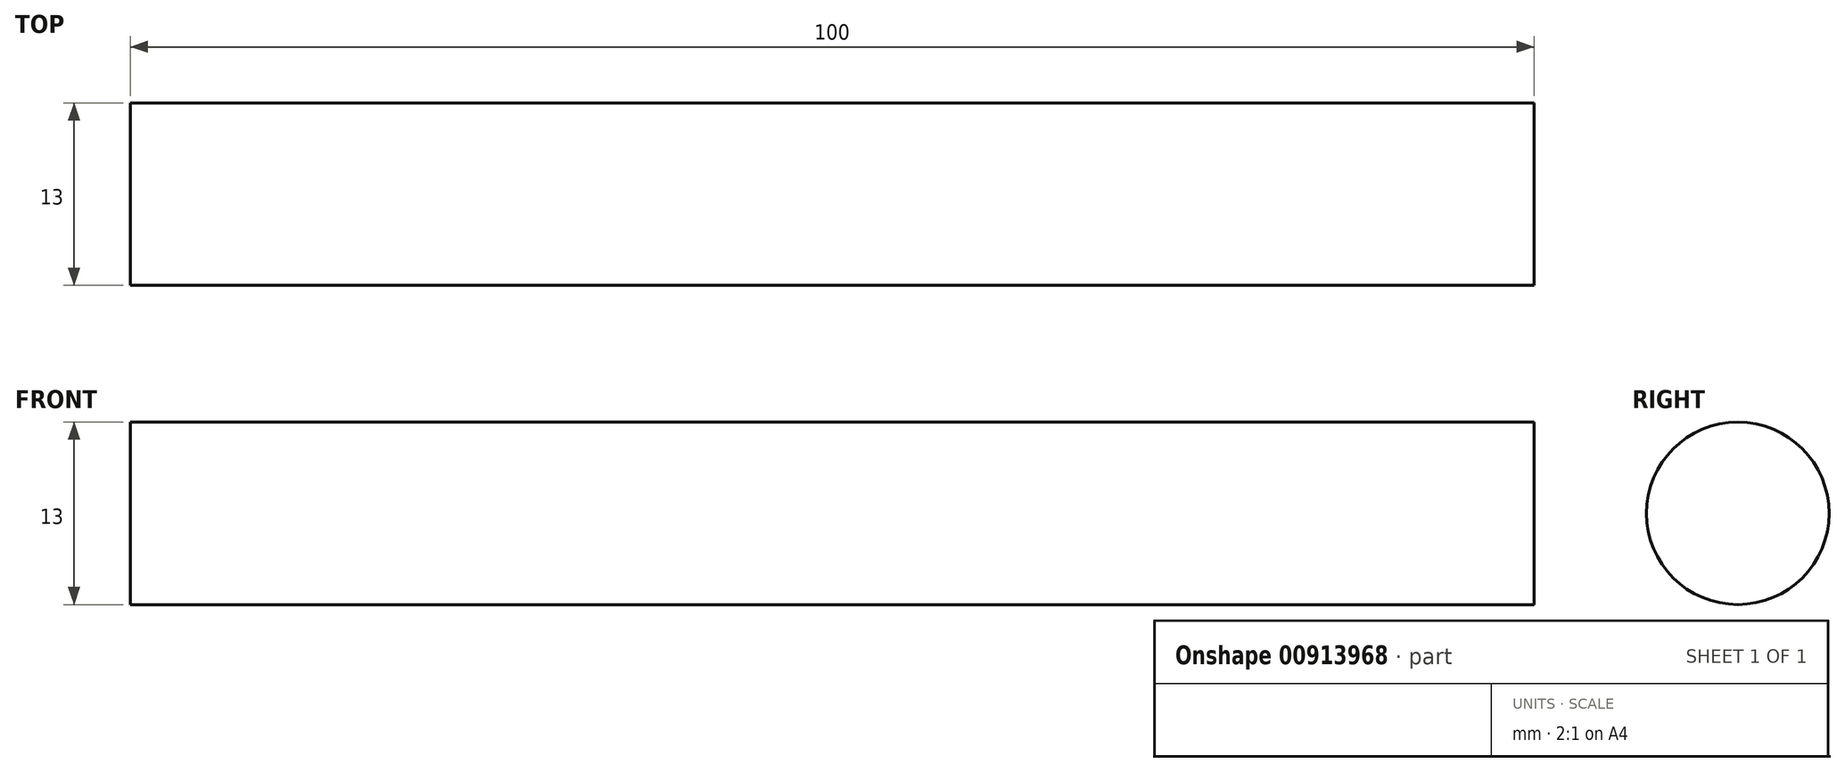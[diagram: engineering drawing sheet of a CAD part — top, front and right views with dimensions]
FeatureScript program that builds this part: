
annotation { "Feature Type Name" : "Feature", "Feature Type Description" : "" }
export const myFeature = defineFeature(function(context is Context, id is Id, definition is map)
    precondition{}
    {
        {
            var Q0;
            Q0=qCreatedBy(makeId("Front.planeOp"),FACE);
            var sketch = newSketch(context, id + "F0", { "sketchPlane" : qUnion([Q0])});
            skLineSegment(sketch, "E0.bottom", {"start": v(-46, 0) * mm, "end": v(54, 0) * mm});
            skLineSegment(sketch, "E0.top", {"start": v(-46, -6.5) * mm, "end": v(54, -6.5) * mm});
            skLineSegment(sketch, "E0.left", {"start": v(-46, 0) * mm, "end": v(-46, -6.5) * mm});
            skLineSegment(sketch, "E0.right", {"start": v(54, 0) * mm, "end": v(54, -6.5) * mm});
            skSolve(sketch);
        }
        {
            var Q0;
            Q0=makeQuery(id+"F0.imprint","IMPRINT",FACE,{"disambiguationData":[TD([[makeQuery(id+"F0.imprint","IMPRINT",EDGE,{"derivedFrom":sQuery(id+"F0.wireOp",EDGE,"E0.bottom")}),-1.0]])]});
            var Q1;
            Q1=sQuery(id+"F0.wireOp",EDGE,"E0.bottom");
            revolve(context, id + "F1", {"surfaceOperationType" : NewSurfaceOperationType.NEW, "entities" : qUnion([Q0]), "axis" : qUnion([Q1]), "revolveType" : RevolveType.FULL});
        }
    });
